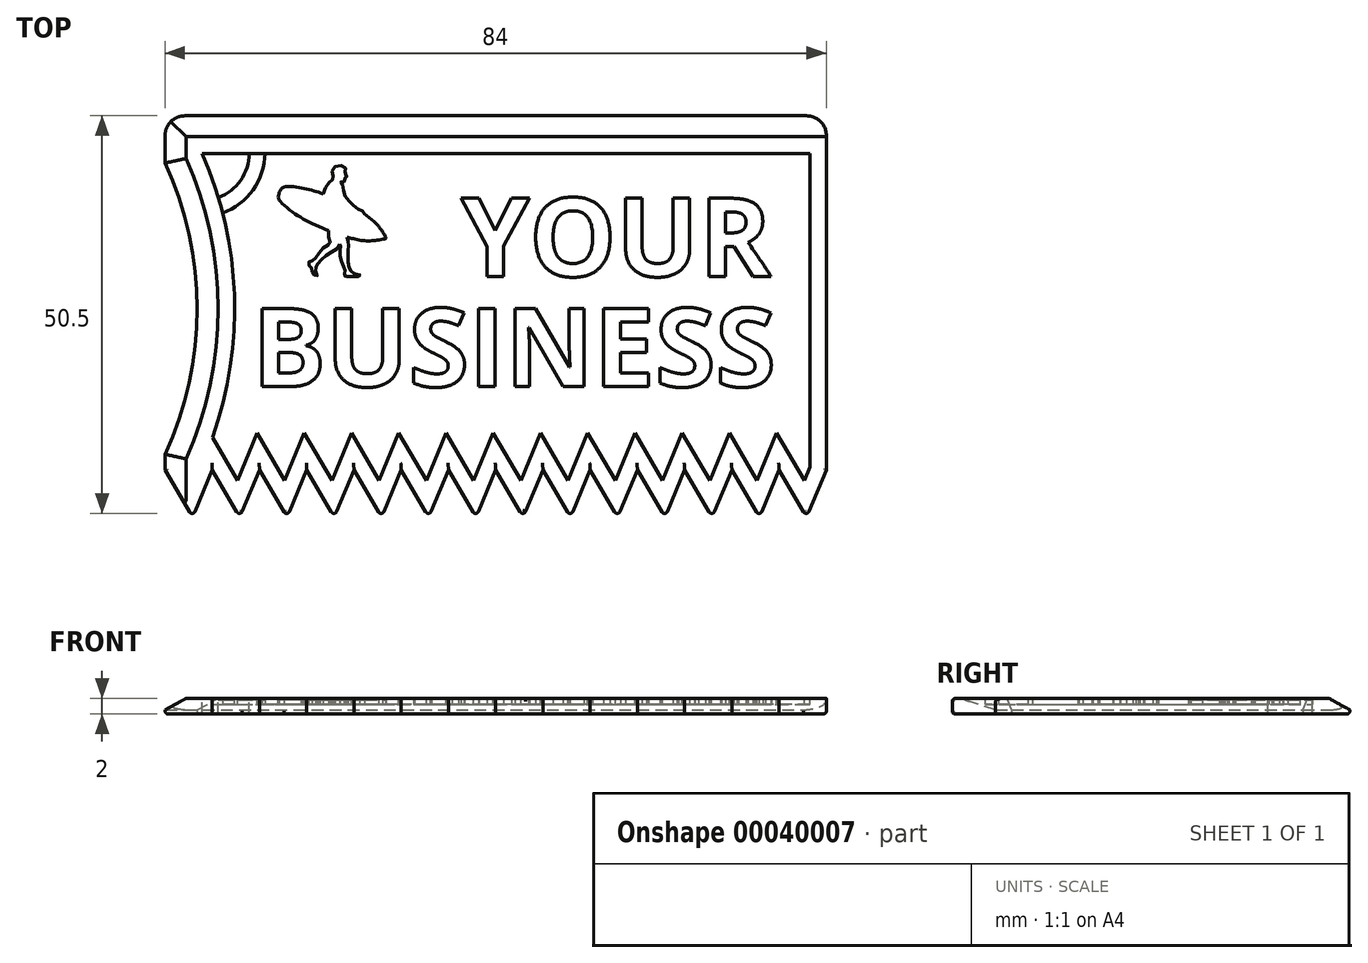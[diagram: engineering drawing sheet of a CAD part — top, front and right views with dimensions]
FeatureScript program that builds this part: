
annotation { "Feature Type Name" : "Feature", "Feature Type Description" : "" }
export const myFeature = defineFeature(function(context is Context, id is Id, definition is map)
    precondition{}
    {
        {
            assignVariable(context, id + "F0", {"name" : "t", "anyValue" : 2});
        }
        {
            var Q0;
            Q0=qCreatedBy(makeId("Top.planeOp"),FACE);
            var sketch = newSketch(context, id + "F1", { "sketchPlane" : qUnion([Q0])});
            skLineSegment(sketch, "E0.bottom", {"start": v(84, 51) * mm, "end": v(0, 51) * mm});
            skLineSegment(sketch, "E0.top", {"start": v(81.5, 0) * mm, "end": v(3.5, 0) * mm, "construction": true});
            skLineSegment(sketch, "E0.left", {"start": v(84, 51) * mm, "end": v(84, 6) * mm});
            skLineSegment(sketch, "E0.right", {"start": v(0, 51) * mm, "end": v(0, 6) * mm, "construction": true});
            skLineSegment(sketch, "E1", {"start": v(84, 6) * mm, "end": v(0, 6) * mm, "construction": true});
            skLineSegment(sketch, "E2", {"start": v(84, 6) * mm, "end": v(81.5, 0) * mm});
            skLineSegment(sketch, "E3", {"start": v(81.5, 0) * mm, "end": v(78, 6) * mm});
            skLineSegment(sketch, "E4.1.0.0", {"start": v(78, 6) * mm, "end": v(75.5, 0) * mm});
            skLineSegment(sketch, "E4.1.0.1", {"start": v(75.5, 0) * mm, "end": v(72, 6) * mm});
            skLineSegment(sketch, "E4.2.0.0", {"start": v(72, 6) * mm, "end": v(69.5, 0) * mm});
            skLineSegment(sketch, "E4.2.0.1", {"start": v(69.5, 0) * mm, "end": v(66, 6) * mm});
            skLineSegment(sketch, "E4.3.0.0", {"start": v(66, 6) * mm, "end": v(63.5, 0) * mm});
            skLineSegment(sketch, "E4.3.0.1", {"start": v(63.5, 0) * mm, "end": v(60, 6) * mm});
            skLineSegment(sketch, "E4.4.0.0", {"start": v(60, 6) * mm, "end": v(57.5, 0) * mm});
            skLineSegment(sketch, "E4.4.0.1", {"start": v(57.5, 0) * mm, "end": v(54, 6) * mm});
            skLineSegment(sketch, "E4.5.0.0", {"start": v(54, 6) * mm, "end": v(51.5, 0) * mm});
            skLineSegment(sketch, "E4.5.0.1", {"start": v(51.5, 0) * mm, "end": v(48, 6) * mm});
            skLineSegment(sketch, "E4.6.0.0", {"start": v(48, 6) * mm, "end": v(45.5, 0) * mm});
            skLineSegment(sketch, "E4.6.0.1", {"start": v(45.5, 0) * mm, "end": v(42, 6) * mm});
            skLineSegment(sketch, "E4.7.0.0", {"start": v(42, 6) * mm, "end": v(39.5, 0) * mm});
            skLineSegment(sketch, "E4.7.0.1", {"start": v(39.5, 0) * mm, "end": v(36, 6) * mm});
            skLineSegment(sketch, "E4.8.0.0", {"start": v(36, 6) * mm, "end": v(33.5, 0) * mm});
            skLineSegment(sketch, "E4.8.0.1", {"start": v(33.5, 0) * mm, "end": v(30, 6) * mm});
            skLineSegment(sketch, "E4.9.0.0", {"start": v(30, 6) * mm, "end": v(27.5, 0) * mm});
            skLineSegment(sketch, "E4.9.0.1", {"start": v(27.5, 0) * mm, "end": v(24, 6) * mm});
            skLineSegment(sketch, "E4.10.0.0", {"start": v(24, 6) * mm, "end": v(21.5, 0) * mm});
            skLineSegment(sketch, "E4.10.0.1", {"start": v(21.5, 0) * mm, "end": v(18, 6) * mm});
            skLineSegment(sketch, "E4.11.0.0", {"start": v(18, 6) * mm, "end": v(15.5, 0) * mm});
            skLineSegment(sketch, "E4.11.0.1", {"start": v(15.5, 0) * mm, "end": v(12, 6) * mm});
            skLineSegment(sketch, "E4.12.0.0", {"start": v(12, 6) * mm, "end": v(9.5, 0) * mm});
            skLineSegment(sketch, "E4.12.0.1", {"start": v(9.5, 0) * mm, "end": v(6, 6) * mm});
            skLineSegment(sketch, "E4.13.0.0", {"start": v(6, 6) * mm, "end": v(3.5, 0) * mm});
            skLineSegment(sketch, "E4.13.0.1", {"start": v(3.5, 0) * mm, "end": v(0, 6) * mm});
            skLineSegment(sketch, "E4.direction1", {"start": v(84, 6) * mm, "end": v(78, 6) * mm, "construction": true});
            skLineSegment(sketch, "E5", {"start": v(0, 6) * mm, "end": v(0, 8) * mm});
            skArc(sketch, "E6", {"start": v(0, 8) * mm, "mid": v(4.07, 26.5) * mm, "end": v(0, 45) * mm});
            skLineSegment(sketch, "E7", {"start": v(0, 45) * mm, "end": v(0, 51) * mm});
            skLineSegment(sketch, "E8", {"start": v(0, 6) * mm, "end": v(0, 0) * mm, "construction": true});
            skSolve(sketch);
        }
        {
            var Q0;
            Q0=qSketchRegion(id+"F1",true);
            extrude(context, id + "F2", {"entities" : qUnion([Q0]), "depth" : (getVariable(context, 't')) * mm});
        }
        {
            var Q0;
            Q0=makeQuery(id+"F2.opExtrude","CAP_EDGE",EDGE,{"disambiguationData":[OSD([sQuery(id+"F1.wireOp",EDGE,"E5")])],"isStart":false});
            var Q1;
            Q1=makeQuery(id+"F2.opExtrude","CAP_EDGE",EDGE,{"disambiguationData":[OSD([sQuery(id+"F1.wireOp",EDGE,"E6")])],"isStart":false});
            var Q2;
            Q2=makeQuery(id+"F2.opExtrude","CAP_EDGE",EDGE,{"disambiguationData":[OSD([sQuery(id+"F1.wireOp",EDGE,"E0.bottom")])],"isStart":false});
            var Q3;
            Q3=makeQuery(id+"F2.opExtrude","CAP_EDGE",EDGE,{"disambiguationData":[OSD([sQuery(id+"F1.wireOp",EDGE,"E7")])],"isStart":false});
            chamfer(context, id + "F3", {"entities" : qUnion([Q0, Q1, Q2, Q3]), "chamferType" : ChamferType.TWO_OFFSETS, "width1" : (getVariable(context, 't') * 2.2 / 3) * mm, "oppositeDirection" : false, "width2" : (getVariable(context, 't') * 4 / 3) * mm, "tangentPropagation" : true});
        }
        {
            var Q0;
            Q0=makeQuery(id+"F2.opExtrude","SWEPT_EDGE",EDGE,{"disambiguationData":[OSD([sQuery(id+"F1.wireOp",EDGE,"E0.bottom"),sQuery(id+"F1.wireOp",EDGE,"E7")])]});
            var Q1;
            Q1=makeQuery(id+"F2.opExtrude","SWEPT_EDGE",EDGE,{"disambiguationData":[OSD([sQuery(id+"F1.wireOp",EDGE,"E0.bottom"),sQuery(id+"F1.wireOp",EDGE,"E0.left")])]});
            fillet(context, id + "F4", {"entities" : qUnion([Q0, Q1]), "radius" : 2.5 * mm, "tangentPropagation" : true, "allowEdgeOverflow" : false});
        }
        {
            var Q0;
            Q0=makeQuery(id+"F2.opExtrude","CAP_FACE",FACE,{"disambiguationData":[OSD([sQuery(id+"F1.wireOp",EDGE,"E0.bottom"),sQuery(id+"F1.wireOp",EDGE,"E0.left"),sQuery(id+"F1.wireOp",EDGE,"E2"),sQuery(id+"F1.wireOp",EDGE,"E3"),sQuery(id+"F1.wireOp",EDGE,"E4.1.0.0"),sQuery(id+"F1.wireOp",EDGE,"E4.1.0.1"),sQuery(id+"F1.wireOp",EDGE,"E4.2.0.0"),sQuery(id+"F1.wireOp",EDGE,"E4.2.0.1"),sQuery(id+"F1.wireOp",EDGE,"E4.3.0.0"),sQuery(id+"F1.wireOp",EDGE,"E4.3.0.1"),sQuery(id+"F1.wireOp",EDGE,"E4.4.0.0"),sQuery(id+"F1.wireOp",EDGE,"E4.4.0.1"),sQuery(id+"F1.wireOp",EDGE,"E4.5.0.0"),sQuery(id+"F1.wireOp",EDGE,"E4.5.0.1"),sQuery(id+"F1.wireOp",EDGE,"E4.6.0.0"),sQuery(id+"F1.wireOp",EDGE,"E4.6.0.1"),sQuery(id+"F1.wireOp",EDGE,"E4.7.0.0"),sQuery(id+"F1.wireOp",EDGE,"E4.7.0.1"),sQuery(id+"F1.wireOp",EDGE,"E4.8.0.0"),sQuery(id+"F1.wireOp",EDGE,"E4.8.0.1"),sQuery(id+"F1.wireOp",EDGE,"E4.9.0.0"),sQuery(id+"F1.wireOp",EDGE,"E4.9.0.1"),sQuery(id+"F1.wireOp",EDGE,"E4.10.0.0"),sQuery(id+"F1.wireOp",EDGE,"E4.10.0.1"),sQuery(id+"F1.wireOp",EDGE,"E4.11.0.0"),sQuery(id+"F1.wireOp",EDGE,"E4.11.0.1"),sQuery(id+"F1.wireOp",EDGE,"E4.12.0.0"),sQuery(id+"F1.wireOp",EDGE,"E4.12.0.1"),sQuery(id+"F1.wireOp",EDGE,"E4.13.0.0"),sQuery(id+"F1.wireOp",EDGE,"E4.13.0.1"),sQuery(id+"F1.wireOp",EDGE,"E5"),sQuery(id+"F1.wireOp",EDGE,"E6"),sQuery(id+"F1.wireOp",EDGE,"E7")])],"isStart":false});
            var sketch = newSketch(context, id + "F5", { "sketchPlane" : qUnion([Q0])});
            skLineSegment(sketch, "E9.0", {"start": v(81.9, 6.42) * mm, "end": v(81.9, 46.23) * mm});
            skLineSegment(sketch, "E9.1", {"start": v(81.19, 4.7) * mm, "end": v(81.9, 6.42) * mm});
            skLineSegment(sketch, "E9.2", {"start": v(77.69, 10.7) * mm, "end": v(81.19, 4.7) * mm});
            skLineSegment(sketch, "E9.3", {"start": v(75.19, 4.7) * mm, "end": v(77.69, 10.7) * mm});
            skLineSegment(sketch, "E9.4", {"start": v(71.69, 10.7) * mm, "end": v(75.19, 4.7) * mm});
            skLineSegment(sketch, "E9.5", {"start": v(69.19, 4.7) * mm, "end": v(71.69, 10.7) * mm});
            skLineSegment(sketch, "E9.6", {"start": v(65.69, 10.7) * mm, "end": v(69.19, 4.7) * mm});
            skLineSegment(sketch, "E9.7", {"start": v(81.9, 46.23) * mm, "end": v(4.67, 46.23) * mm});
            skArc(sketch, "E9.8", {"start": v(4.67, 46.23) * mm, "mid": v(8.8, 28.32) * mm, "end": v(6.02, 10.14) * mm});
            skLineSegment(sketch, "E9.9", {"start": v(6.02, 10.14) * mm, "end": v(9.19, 4.7) * mm});
            skLineSegment(sketch, "E9.10", {"start": v(9.19, 4.7) * mm, "end": v(11.69, 10.7) * mm});
            skLineSegment(sketch, "E9.11", {"start": v(11.69, 10.7) * mm, "end": v(15.19, 4.7) * mm});
            skLineSegment(sketch, "E9.12", {"start": v(15.19, 4.7) * mm, "end": v(17.69, 10.7) * mm});
            skLineSegment(sketch, "E9.13", {"start": v(17.69, 10.7) * mm, "end": v(21.19, 4.7) * mm});
            skLineSegment(sketch, "E9.14", {"start": v(21.19, 4.7) * mm, "end": v(23.69, 10.7) * mm});
            skLineSegment(sketch, "E9.15", {"start": v(23.69, 10.7) * mm, "end": v(27.19, 4.7) * mm});
            skLineSegment(sketch, "E9.16", {"start": v(27.19, 4.7) * mm, "end": v(29.69, 10.7) * mm});
            skLineSegment(sketch, "E9.17", {"start": v(29.69, 10.7) * mm, "end": v(33.19, 4.7) * mm});
            skLineSegment(sketch, "E9.18", {"start": v(33.19, 4.7) * mm, "end": v(35.69, 10.7) * mm});
            skLineSegment(sketch, "E9.19", {"start": v(35.69, 10.7) * mm, "end": v(39.19, 4.7) * mm});
            skLineSegment(sketch, "E9.20", {"start": v(39.19, 4.7) * mm, "end": v(41.69, 10.7) * mm});
            skLineSegment(sketch, "E9.21", {"start": v(41.69, 10.7) * mm, "end": v(45.19, 4.7) * mm});
            skLineSegment(sketch, "E9.22", {"start": v(45.19, 4.7) * mm, "end": v(47.69, 10.7) * mm});
            skLineSegment(sketch, "E9.23", {"start": v(47.69, 10.7) * mm, "end": v(51.19, 4.7) * mm});
            skLineSegment(sketch, "E9.24", {"start": v(51.19, 4.7) * mm, "end": v(53.69, 10.7) * mm});
            skLineSegment(sketch, "E9.25", {"start": v(53.69, 10.7) * mm, "end": v(57.19, 4.7) * mm});
            skLineSegment(sketch, "E9.26", {"start": v(57.19, 4.7) * mm, "end": v(59.69, 10.7) * mm});
            skLineSegment(sketch, "E9.27", {"start": v(59.69, 10.7) * mm, "end": v(63.19, 4.7) * mm});
            skLineSegment(sketch, "E9.28", {"start": v(63.19, 4.7) * mm, "end": v(65.69, 10.7) * mm});
            skSolve(sketch);
        }
        {
            var Q0;
            Q0=makeQuery(id+"F5.imprint","IMPRINT",FACE,{"disambiguationData":[TD([[makeQuery(id+"F5.imprint","IMPRINT",EDGE,{"derivedFrom":sQuery(id+"F5.wireOp",EDGE,"E9.0")}),1.0]])]});
            extrude(context, id + "F6", {"entities" : qUnion([Q0]), "operationType" : NewBodyOperationType.REMOVE, "oppositeDirection" : true, "depth" : (getVariable(context, 't') * 2 / 5) * mm});
        }
        {
            var Q0;
            Q0=makeQuery(id+"F2.opExtrude","CAP_FACE",FACE,{"disambiguationData":[OSD([sQuery(id+"F1.wireOp",EDGE,"E0.bottom"),sQuery(id+"F1.wireOp",EDGE,"E0.left"),sQuery(id+"F1.wireOp",EDGE,"E2"),sQuery(id+"F1.wireOp",EDGE,"E3"),sQuery(id+"F1.wireOp",EDGE,"E4.1.0.0"),sQuery(id+"F1.wireOp",EDGE,"E4.1.0.1"),sQuery(id+"F1.wireOp",EDGE,"E4.2.0.0"),sQuery(id+"F1.wireOp",EDGE,"E4.2.0.1"),sQuery(id+"F1.wireOp",EDGE,"E4.3.0.0"),sQuery(id+"F1.wireOp",EDGE,"E4.3.0.1"),sQuery(id+"F1.wireOp",EDGE,"E4.4.0.0"),sQuery(id+"F1.wireOp",EDGE,"E4.4.0.1"),sQuery(id+"F1.wireOp",EDGE,"E4.5.0.0"),sQuery(id+"F1.wireOp",EDGE,"E4.5.0.1"),sQuery(id+"F1.wireOp",EDGE,"E4.6.0.0"),sQuery(id+"F1.wireOp",EDGE,"E4.6.0.1"),sQuery(id+"F1.wireOp",EDGE,"E4.7.0.0"),sQuery(id+"F1.wireOp",EDGE,"E4.7.0.1"),sQuery(id+"F1.wireOp",EDGE,"E4.8.0.0"),sQuery(id+"F1.wireOp",EDGE,"E4.8.0.1"),sQuery(id+"F1.wireOp",EDGE,"E4.9.0.0"),sQuery(id+"F1.wireOp",EDGE,"E4.9.0.1"),sQuery(id+"F1.wireOp",EDGE,"E4.10.0.0"),sQuery(id+"F1.wireOp",EDGE,"E4.10.0.1"),sQuery(id+"F1.wireOp",EDGE,"E4.11.0.0"),sQuery(id+"F1.wireOp",EDGE,"E4.11.0.1"),sQuery(id+"F1.wireOp",EDGE,"E4.12.0.0"),sQuery(id+"F1.wireOp",EDGE,"E4.12.0.1"),sQuery(id+"F1.wireOp",EDGE,"E4.13.0.0"),sQuery(id+"F1.wireOp",EDGE,"E4.13.0.1"),sQuery(id+"F1.wireOp",EDGE,"E5"),sQuery(id+"F1.wireOp",EDGE,"E6"),sQuery(id+"F1.wireOp",EDGE,"E7")])],"isStart":true});
            var Q1;
            Q1=makeQuery(id+"F2.opExtrude","CAP_EDGE",EDGE,{"disambiguationData":[OSD([sQuery(id+"F1.wireOp",EDGE,"E4.13.0.1")])],"isStart":false});
            var Q2;
            Q2=makeQuery(id+"F2.opExtrude","CAP_EDGE",EDGE,{"disambiguationData":[OSD([sQuery(id+"F1.wireOp",EDGE,"E4.13.0.0")])],"isStart":false});
            var Q3;
            Q3=makeQuery(id+"F2.opExtrude","SWEPT_EDGE",EDGE,{"disambiguationData":[OSD([sQuery(id+"F1.wireOp",EDGE,"E4.13.0.0"),sQuery(id+"F1.wireOp",EDGE,"E4.13.0.1")])]});
            var Q4;
            Q4=makeQuery(id+"F2.opExtrude","CAP_EDGE",EDGE,{"disambiguationData":[OSD([sQuery(id+"F1.wireOp",EDGE,"E4.12.0.1")])],"isStart":false});
            var Q5;
            Q5=makeQuery(id+"F2.opExtrude","SWEPT_EDGE",EDGE,{"disambiguationData":[OSD([sQuery(id+"F1.wireOp",EDGE,"E4.12.0.0"),sQuery(id+"F1.wireOp",EDGE,"E4.12.0.1")])]});
            var Q6;
            Q6=makeQuery(id+"F2.opExtrude","CAP_EDGE",EDGE,{"disambiguationData":[OSD([sQuery(id+"F1.wireOp",EDGE,"E4.12.0.0")])],"isStart":false});
            var Q7;
            Q7=makeQuery(id+"F2.opExtrude","CAP_EDGE",EDGE,{"disambiguationData":[OSD([sQuery(id+"F1.wireOp",EDGE,"E4.11.0.1")])],"isStart":false});
            var Q8;
            Q8=makeQuery(id+"F2.opExtrude","SWEPT_EDGE",EDGE,{"disambiguationData":[OSD([sQuery(id+"F1.wireOp",EDGE,"E4.11.0.0"),sQuery(id+"F1.wireOp",EDGE,"E4.11.0.1")])]});
            var Q9;
            Q9=makeQuery(id+"F2.opExtrude","CAP_EDGE",EDGE,{"disambiguationData":[OSD([sQuery(id+"F1.wireOp",EDGE,"E4.11.0.0")])],"isStart":false});
            var Q10;
            Q10=makeQuery(id+"F2.opExtrude","CAP_EDGE",EDGE,{"disambiguationData":[OSD([sQuery(id+"F1.wireOp",EDGE,"E4.10.0.1")])],"isStart":false});
            var Q11;
            Q11=makeQuery(id+"F2.opExtrude","CAP_EDGE",EDGE,{"disambiguationData":[OSD([sQuery(id+"F1.wireOp",EDGE,"E4.10.0.0")])],"isStart":false});
            var Q12;
            Q12=makeQuery(id+"F2.opExtrude","CAP_EDGE",EDGE,{"disambiguationData":[OSD([sQuery(id+"F1.wireOp",EDGE,"E4.9.0.1")])],"isStart":false});
            var Q13;
            Q13=makeQuery(id+"F2.opExtrude","CAP_EDGE",EDGE,{"disambiguationData":[OSD([sQuery(id+"F1.wireOp",EDGE,"E4.9.0.0")])],"isStart":false});
            var Q14;
            Q14=makeQuery(id+"F2.opExtrude","CAP_EDGE",EDGE,{"disambiguationData":[OSD([sQuery(id+"F1.wireOp",EDGE,"E4.8.0.1")])],"isStart":false});
            var Q15;
            Q15=makeQuery(id+"F2.opExtrude","CAP_EDGE",EDGE,{"disambiguationData":[OSD([sQuery(id+"F1.wireOp",EDGE,"E4.8.0.0")])],"isStart":false});
            var Q16;
            Q16=makeQuery(id+"F2.opExtrude","CAP_EDGE",EDGE,{"disambiguationData":[OSD([sQuery(id+"F1.wireOp",EDGE,"E4.7.0.1")])],"isStart":false});
            var Q17;
            Q17=makeQuery(id+"F2.opExtrude","CAP_EDGE",EDGE,{"disambiguationData":[OSD([sQuery(id+"F1.wireOp",EDGE,"E4.7.0.0")])],"isStart":false});
            var Q18;
            Q18=makeQuery(id+"F2.opExtrude","CAP_EDGE",EDGE,{"disambiguationData":[OSD([sQuery(id+"F1.wireOp",EDGE,"E4.6.0.1")])],"isStart":false});
            var Q19;
            Q19=makeQuery(id+"F2.opExtrude","CAP_EDGE",EDGE,{"disambiguationData":[OSD([sQuery(id+"F1.wireOp",EDGE,"E4.6.0.0")])],"isStart":false});
            var Q20;
            Q20=makeQuery(id+"F2.opExtrude","CAP_EDGE",EDGE,{"disambiguationData":[OSD([sQuery(id+"F1.wireOp",EDGE,"E4.5.0.1")])],"isStart":false});
            var Q21;
            Q21=makeQuery(id+"F2.opExtrude","CAP_EDGE",EDGE,{"disambiguationData":[OSD([sQuery(id+"F1.wireOp",EDGE,"E4.5.0.0")])],"isStart":false});
            var Q22;
            Q22=makeQuery(id+"F2.opExtrude","CAP_EDGE",EDGE,{"disambiguationData":[OSD([sQuery(id+"F1.wireOp",EDGE,"E4.4.0.1")])],"isStart":false});
            var Q23;
            Q23=makeQuery(id+"F2.opExtrude","CAP_EDGE",EDGE,{"disambiguationData":[OSD([sQuery(id+"F1.wireOp",EDGE,"E4.4.0.0")])],"isStart":false});
            var Q24;
            Q24=makeQuery(id+"F2.opExtrude","CAP_EDGE",EDGE,{"disambiguationData":[OSD([sQuery(id+"F1.wireOp",EDGE,"E4.3.0.1")])],"isStart":false});
            var Q25;
            Q25=makeQuery(id+"F2.opExtrude","CAP_EDGE",EDGE,{"disambiguationData":[OSD([sQuery(id+"F1.wireOp",EDGE,"E4.3.0.0")])],"isStart":false});
            var Q26;
            Q26=makeQuery(id+"F2.opExtrude","CAP_EDGE",EDGE,{"disambiguationData":[OSD([sQuery(id+"F1.wireOp",EDGE,"E4.2.0.1")])],"isStart":false});
            var Q27;
            Q27=makeQuery(id+"F2.opExtrude","CAP_EDGE",EDGE,{"disambiguationData":[OSD([sQuery(id+"F1.wireOp",EDGE,"E4.2.0.0")])],"isStart":false});
            var Q28;
            Q28=makeQuery(id+"F2.opExtrude","CAP_EDGE",EDGE,{"disambiguationData":[OSD([sQuery(id+"F1.wireOp",EDGE,"E4.1.0.1")])],"isStart":false});
            var Q29;
            Q29=makeQuery(id+"F2.opExtrude","CAP_EDGE",EDGE,{"disambiguationData":[OSD([sQuery(id+"F1.wireOp",EDGE,"E4.1.0.0")])],"isStart":false});
            var Q30;
            Q30=makeQuery(id+"F2.opExtrude","CAP_EDGE",EDGE,{"disambiguationData":[OSD([sQuery(id+"F1.wireOp",EDGE,"E3")])],"isStart":false});
            var Q31;
            Q31=makeQuery(id+"F2.opExtrude","SWEPT_EDGE",EDGE,{"disambiguationData":[OSD([sQuery(id+"F1.wireOp",EDGE,"E2"),sQuery(id+"F1.wireOp",EDGE,"E3")])]});
            var Q32;
            Q32=makeQuery(id+"F2.opExtrude","CAP_EDGE",EDGE,{"disambiguationData":[OSD([sQuery(id+"F1.wireOp",EDGE,"E2")])],"isStart":false});
            var Q33;
            Q33=makeQuery(id+"F2.opExtrude","SWEPT_EDGE",EDGE,{"disambiguationData":[OSD([sQuery(id+"F1.wireOp",EDGE,"E4.1.0.0"),sQuery(id+"F1.wireOp",EDGE,"E4.1.0.1")])]});
            var Q34;
            Q34=makeQuery(id+"F2.opExtrude","SWEPT_EDGE",EDGE,{"disambiguationData":[OSD([sQuery(id+"F1.wireOp",EDGE,"E4.2.0.0"),sQuery(id+"F1.wireOp",EDGE,"E4.2.0.1")])]});
            var Q35;
            Q35=makeQuery(id+"F2.opExtrude","SWEPT_EDGE",EDGE,{"disambiguationData":[OSD([sQuery(id+"F1.wireOp",EDGE,"E4.3.0.0"),sQuery(id+"F1.wireOp",EDGE,"E4.3.0.1")])]});
            var Q36;
            Q36=makeQuery(id+"F2.opExtrude","SWEPT_EDGE",EDGE,{"disambiguationData":[OSD([sQuery(id+"F1.wireOp",EDGE,"E4.4.0.0"),sQuery(id+"F1.wireOp",EDGE,"E4.4.0.1")])]});
            var Q37;
            Q37=makeQuery(id+"F2.opExtrude","SWEPT_EDGE",EDGE,{"disambiguationData":[OSD([sQuery(id+"F1.wireOp",EDGE,"E4.5.0.0"),sQuery(id+"F1.wireOp",EDGE,"E4.5.0.1")])]});
            var Q38;
            Q38=makeQuery(id+"F2.opExtrude","SWEPT_EDGE",EDGE,{"disambiguationData":[OSD([sQuery(id+"F1.wireOp",EDGE,"E4.6.0.0"),sQuery(id+"F1.wireOp",EDGE,"E4.6.0.1")])]});
            var Q39;
            Q39=makeQuery(id+"F2.opExtrude","SWEPT_EDGE",EDGE,{"disambiguationData":[OSD([sQuery(id+"F1.wireOp",EDGE,"E4.7.0.0"),sQuery(id+"F1.wireOp",EDGE,"E4.7.0.1")])]});
            var Q40;
            Q40=makeQuery(id+"F2.opExtrude","SWEPT_EDGE",EDGE,{"disambiguationData":[OSD([sQuery(id+"F1.wireOp",EDGE,"E4.8.0.0"),sQuery(id+"F1.wireOp",EDGE,"E4.8.0.1")])]});
            var Q41;
            Q41=makeQuery(id+"F2.opExtrude","SWEPT_EDGE",EDGE,{"disambiguationData":[OSD([sQuery(id+"F1.wireOp",EDGE,"E4.9.0.0"),sQuery(id+"F1.wireOp",EDGE,"E4.9.0.1")])]});
            var Q42;
            Q42=makeQuery(id+"F2.opExtrude","SWEPT_EDGE",EDGE,{"disambiguationData":[OSD([sQuery(id+"F1.wireOp",EDGE,"E4.10.0.0"),sQuery(id+"F1.wireOp",EDGE,"E4.10.0.1")])]});
            fillet(context, id + "F7", {"entities" : qUnion([Q0, Q1, Q2, Q3, Q4, Q5, Q6, Q7, Q8, Q9, Q10, Q11, Q12, Q13, Q14, Q15, Q16, Q17, Q18, Q19, Q20, Q21, Q22, Q23, Q24, Q25, Q26, Q27, Q28, Q29, Q30, Q31, Q32, Q33, Q34, Q35, Q36, Q37, Q38, Q39, Q40, Q41, Q42]), "radius" : .4 * mm, "tangentPropagation" : true, "allowEdgeOverflow" : false});
        }
        {
            var Q0;
            Q0=makeQuery(id+"F6.boolean.opBoolean","COPY",FACE,{"derivedFrom":makeQuery(id+"F6.opExtrude","CAP_FACE",FACE,{"disambiguationData":[OSD([sQuery(id+"F5.wireOp",EDGE,"E9.0"),sQuery(id+"F5.wireOp",EDGE,"E9.1"),sQuery(id+"F5.wireOp",EDGE,"E9.2"),sQuery(id+"F5.wireOp",EDGE,"E9.3"),sQuery(id+"F5.wireOp",EDGE,"E9.4"),sQuery(id+"F5.wireOp",EDGE,"E9.5"),sQuery(id+"F5.wireOp",EDGE,"E9.6"),sQuery(id+"F5.wireOp",EDGE,"E9.7"),sQuery(id+"F5.wireOp",EDGE,"E9.8"),sQuery(id+"F5.wireOp",EDGE,"E9.9"),sQuery(id+"F5.wireOp",EDGE,"E9.10"),sQuery(id+"F5.wireOp",EDGE,"E9.11"),sQuery(id+"F5.wireOp",EDGE,"E9.12"),sQuery(id+"F5.wireOp",EDGE,"E9.13"),sQuery(id+"F5.wireOp",EDGE,"E9.14"),sQuery(id+"F5.wireOp",EDGE,"E9.15"),sQuery(id+"F5.wireOp",EDGE,"E9.16"),sQuery(id+"F5.wireOp",EDGE,"E9.17"),sQuery(id+"F5.wireOp",EDGE,"E9.18"),sQuery(id+"F5.wireOp",EDGE,"E9.19"),sQuery(id+"F5.wireOp",EDGE,"E9.20"),sQuery(id+"F5.wireOp",EDGE,"E9.21"),sQuery(id+"F5.wireOp",EDGE,"E9.22"),sQuery(id+"F5.wireOp",EDGE,"E9.23"),sQuery(id+"F5.wireOp",EDGE,"E9.24"),sQuery(id+"F5.wireOp",EDGE,"E9.25"),sQuery(id+"F5.wireOp",EDGE,"E9.26"),sQuery(id+"F5.wireOp",EDGE,"E9.27"),sQuery(id+"F5.wireOp",EDGE,"E9.28")])],"isStart":false})});
            var sketch = newSketch(context, id + "F8", { "sketchPlane" : qUnion([Q0])});
            skText(sketch, "E10", { "text": "BUSINESS", "fontName": "OpenSans-Bold.ttf"});
            skText(sketch, "E11", { "text": "YOUR", "fontName": "OpenSans-Bold.ttf"});
            const initialGuessF8  = {"E10": [0.0111, 0.01661, 1, 0, 0.01], "E11": [0.0376, 0.03061, 1, 0, 0.01]};
            skSetInitialGuess(sketch, initialGuessF8);
            skSolve(sketch);
        }
        {
            var Q0;
            Q0=makeQuery(id+"F8.imprint","IMPRINT",FACE,{"disambiguationData":[TD([[makeQuery(id+"F8.imprint","IMPRINT",EDGE,{"derivedFrom":sQuery(id+"F8.wireOp",EDGE,"E10.sketch_text.stroke-0")}),1.0]])]});
            var sketch = newSketch(context, id + "F9", { "sketchPlane" : qUnion([Q0])});
            skLineSegment(sketch, "E12.0", {"start": v(81.9, 46.23) * mm, "end": v(4.67, 46.23) * mm});
            skArc(sketch, "E12.1", {"start": v(4.67, 46.23) * mm, "mid": v(8.8, 28.32) * mm, "end": v(6.02, 10.14) * mm});
            skPoint(sketch, "E12.2", {"position": v(4.67, 46.23) * mm});
            skArc(sketch, "E13", {"start": v(6.76, 40.6) * mm, "mid": v(9.6, 42.8) * mm, "end": v(10.67, 46.23) * mm});
            skArc(sketch, "E14", {"start": v(7.3, 38.68) * mm, "mid": v(11.2, 41.6) * mm, "end": v(12.67, 46.23) * mm});
            skLineSegment(sketch, "E15", {"start": v(14.33, 41.37) * mm, "end": v(28.35, 35.34) * mm, "construction": true});
            skFitSpline(sketch, "E16", {"points": [v(20.78, 36.4) * mm, v(18.17, 37.57) * mm, v(16.2, 38.77) * mm, v(14.57, 40.2) * mm, v(14.39, 40.75) * mm, v(14.51, 41.3) * mm], "startDerivative": vector(-8.18, 3.62) * mm, "endDerivative": vector(1.44, 4.42) * mm});
            skFitSpline(sketch, "E17", {"points": [v(21.8, 40.38) * mm, v(19.73, 41.2) * mm, v(17.5, 41.8) * mm, v(15.34, 42) * mm, v(14.82, 41.76) * mm, v(14.51, 41.3) * mm], "startDerivative": vector(-8.26, 3.44) * mm, "endDerivative": vector(-2.21, -4.08) * mm});
            skFitSpline(sketch, "E18", {"points": [v(20.78, 36.4) * mm, v(20.78, 35.64) * mm, v(20.95, 35.07) * mm, v(20.96, 34.8) * mm, v(20.8, 34.66) * mm, v(20.25, 34.4) * mm, v(19.79, 33.88) * mm, v(19.35, 33.26) * mm, v(19, 32.82) * mm, v(18.79, 32.65) * mm, v(18.48, 32.52) * mm, v(18.27, 32.44) * mm, v(18.2, 32.27) * mm, v(18.32, 31.93) * mm, v(18.48, 31.77) * mm, v(18.61, 31.65) * mm, v(18.65, 31.45) * mm, v(18.68, 31.05) * mm, v(18.84, 30.85) * mm, v(19.05, 30.74) * mm, v(19.33, 30.68) * mm, v(19.38, 30.7) * mm, v(19.39, 30.75) * mm, v(19.36, 30.83) * mm, v(19.24, 30.92) * mm, v(19.13, 31.03) * mm, v(19.11, 31.31) * mm, v(19.14, 31.62) * mm, v(19.17, 31.85) * mm, v(19.25, 32.01) * mm, v(19.45, 32.31) * mm, v(19.98, 32.83) * mm, v(20.57, 33.32) * mm, v(21.18, 33.76) * mm, v(21.73, 34.08) * mm, v(21.96, 34.28) * mm, v(22.05, 34.5) * mm, v(22.1, 34.7) * mm, v(22.15, 34.73) * mm, v(22.18, 34.73) * mm], "startDerivative": vector(-1.7, -19.21) * mm, "endDerivative": vector(3.01, -1.59) * mm});
            skFitSpline(sketch, "E19", {"points": [v(20.05, 41.08) * mm, v(20.31, 41.73) * mm, v(20.57, 42.25) * mm, v(20.85, 42.54) * mm, v(21.15, 42.79) * mm, v(21.36, 42.97) * mm, v(21.42, 43.1) * mm, v(21.3, 43.35) * mm, v(21.2, 43.69) * mm, v(21.26, 44.09) * mm, v(21.42, 44.41) * mm, v(21.96, 44.72) * mm, v(22.41, 44.65) * mm, v(22.73, 44.52) * mm, v(22.95, 44.3) * mm, v(22.93, 44.07) * mm, v(22.87, 43.95) * mm, v(22.93, 43.83) * mm, v(22.96, 43.68) * mm, v(22.91, 43.6) * mm, v(22.9, 43.54) * mm, v(22.98, 43.43) * mm, v(23.06, 43.31) * mm, v(23.06, 43.23) * mm, v(23.02, 43.17) * mm, v(22.9, 43.2) * mm, v(22.89, 43.13) * mm, v(22.89, 43.03) * mm, v(22.86, 42.96) * mm, v(22.81, 42.9) * mm, v(22.82, 42.8) * mm, v(22.85, 42.72) * mm, v(22.83, 42.65) * mm, v(22.74, 42.62) * mm, v(22.65, 42.58) * mm, v(22.47, 42.6) * mm, v(22.37, 42.6) * mm, v(22.3, 42.56) * mm, v(22.37, 42.46) * mm, v(22.53, 42.3) * mm, v(22.67, 41.97) * mm, v(22.68, 41.44) * mm, v(22.8, 40.96) * mm, v(23.02, 40.5) * mm, v(23.5, 40.04) * mm, v(23.89, 39.68) * mm, v(24.31, 39.38) * mm, v(24.62, 39.05) * mm, v(24.88, 38.93) * mm, v(25.2, 38.8) * mm, v(25.31, 38.6) * mm, v(25.34, 38.5) * mm], "startDerivative": vector(7.84, 19.36) * mm, "endDerivative": vector(2.4, -8.81) * mm});
            skFitSpline(sketch, "E20", {"points": [v(23.11, 35.6) * mm, v(23.77, 35.42) * mm, v(24.73, 35.21) * mm, v(25.68, 35.1) * mm, v(26.5, 35.15) * mm, v(27.4, 35.27) * mm, v(28.03, 35.44) * mm, v(28.05, 35.47) * mm], "startDerivative": vector(4.26, -1.27) * mm, "endDerivative": vector(0.24, 0.98) * mm});
            skFitSpline(sketch, "E21.MirrorCS", {"points": [v(24.56, 38.97) * mm, v(25.15, 38.62) * mm, v(25.96, 38.06) * mm, v(26.68, 37.45) * mm, v(27.23, 36.82) * mm, v(27.75, 36.09) * mm, v(28.06, 35.52) * mm, v(28.05, 35.47) * mm], "startDerivative": vector(3.85, -2.22) * mm, "endDerivative": vector(-0.55, -0.85) * mm});
            skFitSpline(sketch, "E22", {"points": [v(23.11, 35.6) * mm, v(23.22, 35.14) * mm, v(23.28, 34.82) * mm, v(23.26, 34.39) * mm, v(23.22, 33.76) * mm, v(23.23, 33.07) * mm, v(23.28, 32.27) * mm, v(23.41, 31.6) * mm, v(23.57, 31.3) * mm, v(23.85, 31.1) * mm, v(24.1, 30.94) * mm, v(24.4, 30.87) * mm, v(24.63, 30.85) * mm, v(24.73, 30.83) * mm, v(24.73, 30.75) * mm, v(24.68, 30.67) * mm, v(24.57, 30.62) * mm, v(24.4, 30.58) * mm, v(24.1, 30.57) * mm, v(23.65, 30.57) * mm, v(23.34, 30.59) * mm, v(23.1, 30.58) * mm, v(22.93, 30.59) * mm, v(22.84, 30.63) * mm, v(22.8, 30.76) * mm, v(22.8, 30.93) * mm, v(22.87, 31.1) * mm, v(22.87, 31.29) * mm, v(22.75, 31.62) * mm, v(22.54, 32.2) * mm, v(22.35, 32.86) * mm, v(22.2, 33.51) * mm, v(22.26, 34.1) * mm, v(22.28, 34.5) * mm, v(22.26, 34.67) * mm, v(22.18, 34.73) * mm], "startDerivative": vector(2.94, -13.83) * mm, "endDerivative": vector(-5.6, 2.93) * mm});
            skSolve(sketch);
        }
        {
            var Q0;
            Q0 = qSketchRegion(id + "F8", true);
            var Q1;
            Q1=makeQuery(id+"F2.opExtrude","CAP_FACE",FACE,{"disambiguationData":[OSD([sQuery(id+"F1.wireOp",EDGE,"E0.bottom"),sQuery(id+"F1.wireOp",EDGE,"E0.left"),sQuery(id+"F1.wireOp",EDGE,"E2"),sQuery(id+"F1.wireOp",EDGE,"E3"),sQuery(id+"F1.wireOp",EDGE,"E4.1.0.0"),sQuery(id+"F1.wireOp",EDGE,"E4.1.0.1"),sQuery(id+"F1.wireOp",EDGE,"E4.2.0.0"),sQuery(id+"F1.wireOp",EDGE,"E4.2.0.1"),sQuery(id+"F1.wireOp",EDGE,"E4.3.0.0"),sQuery(id+"F1.wireOp",EDGE,"E4.3.0.1"),sQuery(id+"F1.wireOp",EDGE,"E4.4.0.0"),sQuery(id+"F1.wireOp",EDGE,"E4.4.0.1"),sQuery(id+"F1.wireOp",EDGE,"E4.5.0.0"),sQuery(id+"F1.wireOp",EDGE,"E4.5.0.1"),sQuery(id+"F1.wireOp",EDGE,"E4.6.0.0"),sQuery(id+"F1.wireOp",EDGE,"E4.6.0.1"),sQuery(id+"F1.wireOp",EDGE,"E4.7.0.0"),sQuery(id+"F1.wireOp",EDGE,"E4.7.0.1"),sQuery(id+"F1.wireOp",EDGE,"E4.8.0.0"),sQuery(id+"F1.wireOp",EDGE,"E4.8.0.1"),sQuery(id+"F1.wireOp",EDGE,"E4.9.0.0"),sQuery(id+"F1.wireOp",EDGE,"E4.9.0.1"),sQuery(id+"F1.wireOp",EDGE,"E4.10.0.0"),sQuery(id+"F1.wireOp",EDGE,"E4.10.0.1"),sQuery(id+"F1.wireOp",EDGE,"E4.11.0.0"),sQuery(id+"F1.wireOp",EDGE,"E4.11.0.1"),sQuery(id+"F1.wireOp",EDGE,"E4.12.0.0"),sQuery(id+"F1.wireOp",EDGE,"E4.12.0.1"),sQuery(id+"F1.wireOp",EDGE,"E4.13.0.0"),sQuery(id+"F1.wireOp",EDGE,"E4.13.0.1"),sQuery(id+"F1.wireOp",EDGE,"E5"),sQuery(id+"F1.wireOp",EDGE,"E6"),sQuery(id+"F1.wireOp",EDGE,"E7")])],"isStart":false});
            extrude(context, id + "F10", {"entities" : qUnion([Q0]), "operationType" : NewBodyOperationType.ADD, "endBound" : BoundingType.UP_TO_SURFACE, "endBoundEntityFace" : qUnion([Q1]), "depth" : 25 * mm});
        }
        {
            var Q0;
            {var subQ3=sQuery(id+"F9.wireOp",EDGE,"E13");Q0=makeQuery(id+"F9.imprint","IMPRINT",FACE,{"disambiguationData":[TD([[makeQuery(id+"F9.imprint","IMPRINT",EDGE,{"derivedFrom":subQ3}),1.0]])]});}
            extrude(context, id + "F11", {"entities" : qUnion([Q0]), "operationType" : NewBodyOperationType.REMOVE, "oppositeDirection" : true, "depth" : 25 * mm});
        }
        {
            var Q0;
            {var subQ0=sQuery(id+"F9.wireOp",EDGE,"E13");Q0=makeQuery(id+"F9.imprint","IMPRINT",FACE,{"disambiguationData":[TD([[makeQuery(id+"F9.imprint","IMPRINT",EDGE,{"derivedFrom":subQ0}),-1.0]])]});}
            var Q1;
            Q1=makeQuery(id+"F9.imprint","IMPRINT",FACE,{"disambiguationData":[TD([[makeQuery(id+"F9.imprint","IMPRINT",EDGE,{"derivedFrom":sQuery(id+"F9.wireOp",EDGE,"E16")}),-1.0]])]});
            extrude(context, id + "F12", {"entities" : qUnion([Q0, Q1]), "operationType" : NewBodyOperationType.ADD, "depth" : .6 * mm});
        }
    });
